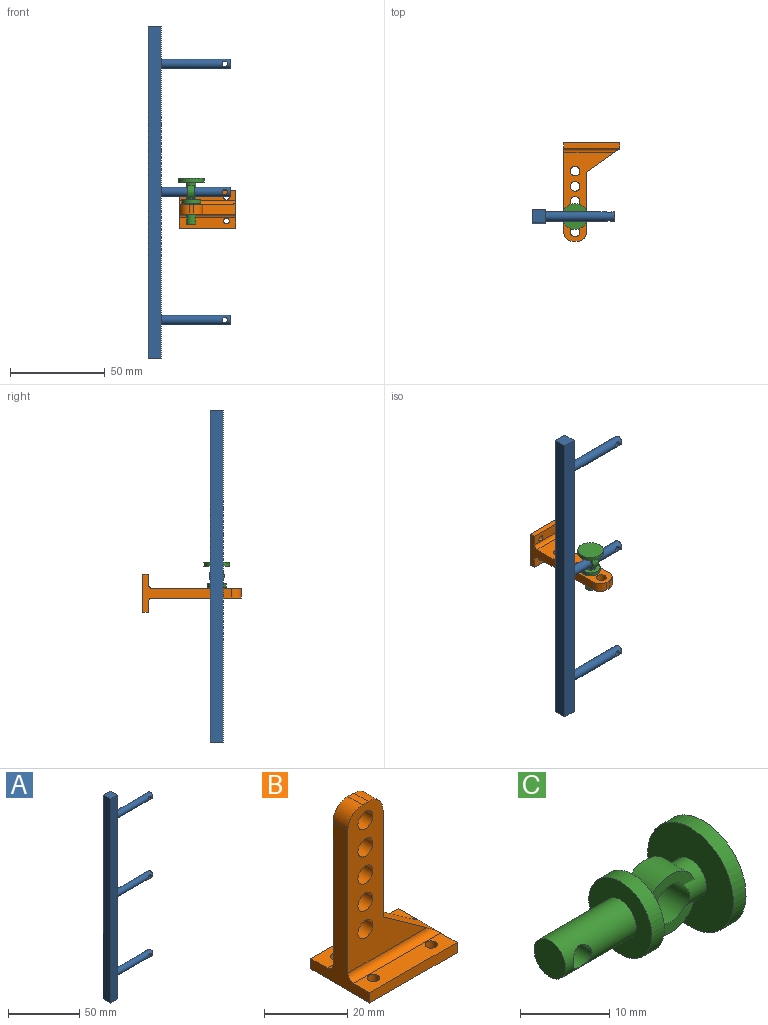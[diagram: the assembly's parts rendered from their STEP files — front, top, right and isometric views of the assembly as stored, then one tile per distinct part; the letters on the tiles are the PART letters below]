
ASSEMBLY  parts=3 mates=2
PART A: 15 faces, bbox 43.5x7x175 mm
  f0: cylinder r=2.5mm len=36.5mm, axis (-1,0,0), area 558.5mm2, adj f3,f5,f14
  f1: cylinder r=2.5mm len=36.5mm, axis (-1,0,0), area 558.5mm2, adj f5,f8,f13
  f2: cylinder r=2.46mm len=36.5mm, axis (-1,0,0), area 550.2mm2, adj f5,f11,f12
  f3: plane 5x5mm, normal (1,0,0), area 19.6mm2, adj f0
  f4: plane 175x7mm, normal (0,-1,0), area 1225mm2, adj f5,f7,f9,f10
  f5: plane 175x7mm, normal (1,0,0), area 1166.7mm2, adj f0,f1,f2,f4,f6,f9,f10
  f6: plane 175x7mm, normal (0,1,0), area 1225mm2, adj f5,f7,f9,f10
  f7: plane 175x7mm, normal (-1,0,0), area 1225mm2, adj f4,f6,f9,f10
  f8: plane 5x5mm, normal (1,0,0), area 19.6mm2, adj f1
  f9: plane 7x7mm, normal (0,0,1), area 49mm2, adj f4,f5,f6,f7
  f10: plane 7x7mm, normal (0,0,-1), area 49mm2, adj f4,f5,f6,f7
  f11: plane 4.93x4.93mm, normal (1,0,0), area 19.1mm2, adj f2
  f12: cylinder r=1.5mm len=4.93mm, axis (0,1,0), area 41.8mm2, adj f2
  f13: cylinder r=1.5mm len=5mm, axis (0,1,0), area 42.5mm2, adj f1
  f14: cylinder r=1.5mm len=5mm, axis (0,1,0), area 42.5mm2, adj f0
PART B: 25 faces, bbox 29.6x20x52 mm
  f0: plane 29.61x5.5mm, normal (0,0,1), area 148.7mm2, adj f2,f4,f6,f17,f20,f24
  f1: plane 29.61x5.5mm, normal (0,0,1), area 148.7mm2, adj f2,f4,f5,f18,f19,f23
  f2: plane 47x20mm, normal (-1,0,0), area 281.7mm2, adj f0,f1,f3,f5,f6,f15,f16,f22
  f3: plane 29.61x20mm, normal (0,0,-1), area 563.9mm2, adj f2,f4,f5,f6,f17,f18,f19,f20
  f4: plane 20x3mm, normal (1,0,0), area 60mm2, adj f0,f1,f3,f5,f6,f7
  f5: plane 29.61x3mm, normal (0,-1,0), area 88.8mm2, adj f1,f2,f3,f4
  f6: plane 29.61x3mm, normal (0,1,0), area 88.8mm2, adj f0,f2,f3,f4
  f7: plane 17.61x12.6mm, normal (0.58,0,0.81), area 111.2mm2, adj f4,f8,f15,f16,f23,f24
  f8: plane 31.4x5mm, normal (1,0,0), area 157mm2, adj f7,f15,f16,f21
  f9: plane 5x2mm, normal (0,0,1), area 10mm2, adj f15,f16,f21,f22
  f10: cylinder r=2.55mm len=5.1mm, axis (0,1,0), area 80.1mm2, adj f15,f16
  f11: cylinder r=2.55mm len=5.1mm, axis (0,1,0), area 80.1mm2, adj f15,f16
  f12: cylinder r=2.55mm len=5.1mm, axis (0,1,0), area 80.1mm2, adj f15,f16
  f13: cylinder r=2.55mm len=5.1mm, axis (0,1,0), area 80.1mm2, adj f15,f16
  f14: cylinder r=2.55mm len=5.1mm, axis (0,1,0), area 80.1mm2, adj f15,f16
  f15: plane 47x26.82mm, normal (0,-1,0), area 529.7mm2, adj f2,f7,f8,f9,f10,f11,f12,f13
  f16: plane 47x26.82mm, normal (0,1,0), area 529.7mm2, adj f2,f7,f8,f9,f10,f11,f12,f13
  f17: cylinder r=1.5mm len=3mm, axis (0,0,1), area 28.3mm2, adj f0,f3
  f18: cylinder r=1.5mm len=3mm, axis (0,0,1), area 28.3mm2, adj f1,f3
  f19: cylinder r=1.5mm len=3mm, axis (0,0,1), area 28.3mm2, adj f1,f3
  f20: cylinder r=1.5mm len=3mm, axis (0,0,1), area 28.3mm2, adj f0,f3
  f21: cylinder r=5mm len=5mm, axis (0,1,0), area 39.3mm2, adj f8,f9,f15,f16
  f22: cylinder r=5mm len=5mm, axis (0,1,0), area 39.3mm2, adj f2,f9,f15,f16
  f23: cylinder r=2mm len=29.61mm, axis (-1,0,0), area 89.8mm2, adj f1,f2,f7,f15
  f24: cylinder r=2mm len=29.61mm, axis (1,0,0), area 89.8mm2, adj f0,f2,f7,f16
PART C: 18 faces, bbox 24.4x13.6x13.6 mm
  f0: cylinder r=2.5mm len=5mm, axis (-1,0,0), area 34.5mm2, adj f4,f11,f12,f13,f14,f15,f16,f17
  f1: cylinder r=2.5mm len=5mm, axis (-1,0,0), area 16.4mm2, adj f5,f11,f12,f13,f14,f15,f16,f17
  f2: plane 13.6x13.6mm, normal (1,0,0), area 145.2mm2, adj f3
  f3: cylinder r=6.8mm len=13.6mm, axis (-1,0,0), area 85.4mm2, adj f2,f4
  f4: plane 13.6x13.6mm, normal (-1,0,0), area 125.6mm2, adj f0,f3
  f5: plane 10x10mm, normal (1,0,0), area 58.9mm2, adj f1,f6
  f6: cylinder r=5mm len=10mm, axis (-1,0,0), area 62.8mm2, adj f5,f7
  f7: plane 10x10mm, normal (-1,0,0), area 58.9mm2, adj f6,f8
  f8: cylinder r=2.5mm len=11.21mm, axis (-1,0,0), area 161.2mm2, adj f7,f9,f10
  f9: plane 5x5mm, normal (-1,0,0), area 19.6mm2, adj f8
  f10: cylinder r=1.5mm len=5mm, axis (0,-1,0), area 42.5mm2, adj f8
  f11: plane 7.42x2.5mm, normal (0,1,0), area 10.4mm2, adj f0,f1,f13,f17
  f12: plane 7.42x2.5mm, normal (0,-1,0), area 10.4mm2, adj f0,f1,f13,f17
  f13: cylinder r=4mm len=7.42mm, axis (0,1,0), area 31.6mm2, adj f0,f1,f11,f12
  f14: plane 7.42x2.5mm, normal (0,-1,0), area 10.4mm2, adj f0,f1,f16,f17
  f15: plane 7.42x2.5mm, normal (0,1,0), area 10.4mm2, adj f0,f1,f16,f17
  f16: cylinder r=4mm len=7.42mm, axis (0,1,0), area 31.6mm2, adj f0,f1,f14,f15
  f17: cylinder r=2.55mm len=5.1mm, axis (0,1,0), area 68.3mm2, adj f0,f1,f11,f12,f14,f15
PLACE A t=(-56.92,9.37,-14.96)mm
PLACE B rot(axis=(1,0,0),90deg) t=(-28.95,21.37,38.44)mm
PLACE C rot(axis=(0.58,-0.58,0.58),120deg) t=(-37.71,9.37,43.54)mm
MATE slider C.f17 <-> A.f1  axis (-1,0,0) through (-35.17,9.37,47.54)mm
MATE revolute B.f12 <-> C.f0  axis (0,0,-1) through (-37.71,9.37,35.94)mm
